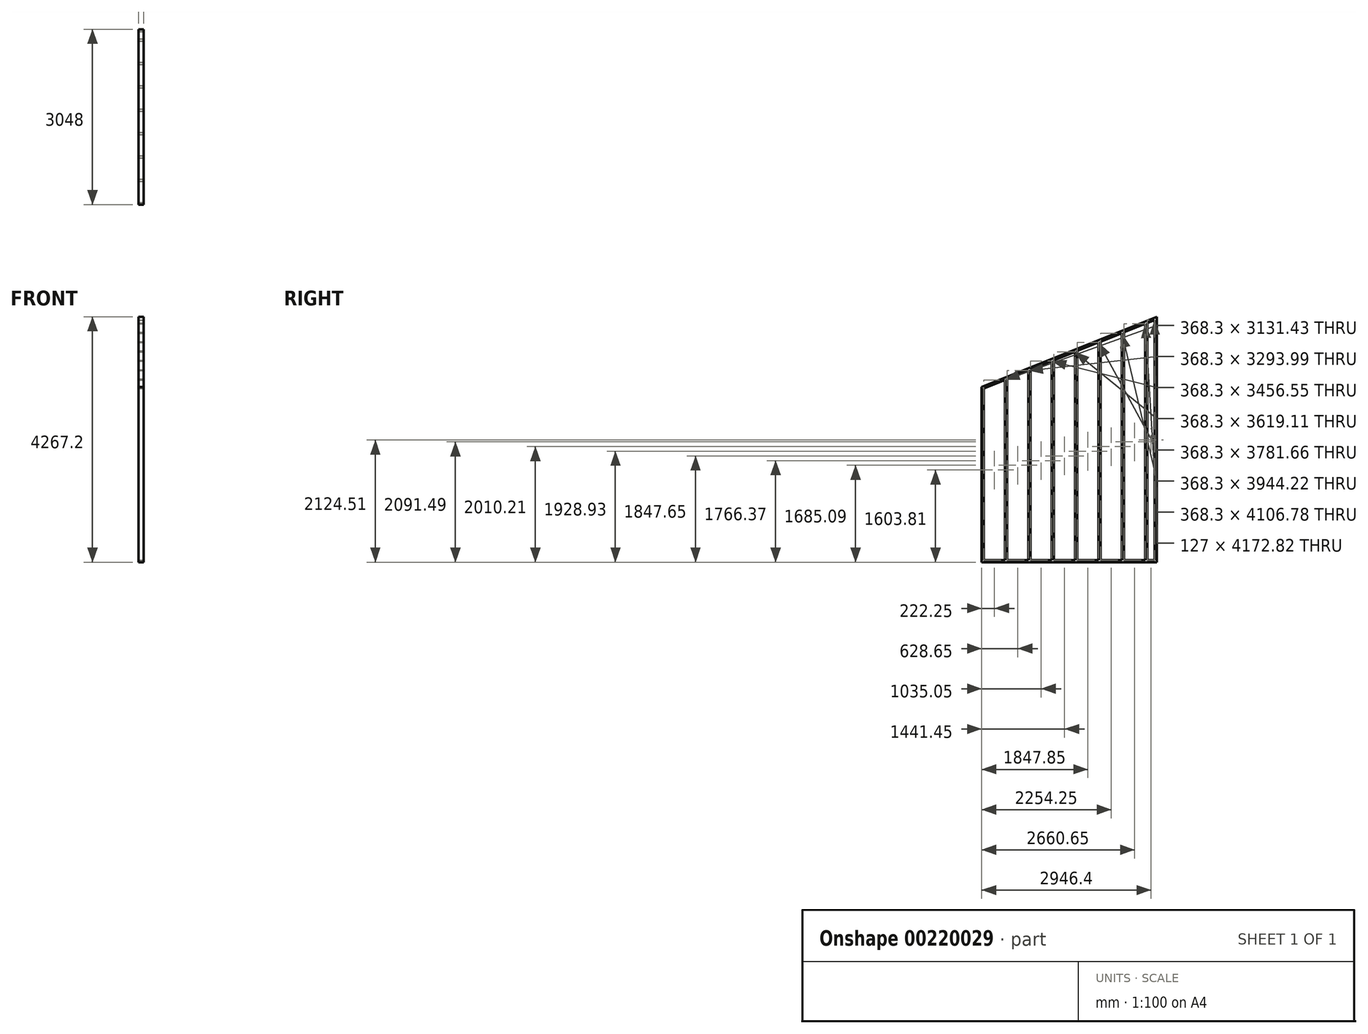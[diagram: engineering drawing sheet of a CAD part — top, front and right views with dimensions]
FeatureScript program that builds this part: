
annotation { "Feature Type Name" : "Feature", "Feature Type Description" : "" }
export const myFeature = defineFeature(function(context is Context, id is Id, definition is map)
    precondition{}
    {
        {
            var Q0;
            Q0=qCreatedBy(makeId("Right.planeOp"),FACE);
            var sketch = newSketch(context, id + "F0", { "sketchPlane" : qUnion([Q0])});
            skLineSegment(sketch, "E0", {"start": v(0, 0) * mm, "end": v(3048, 0) * mm});
            skLineSegment(sketch, "E1", {"start": v(3048, 0) * mm, "end": v(3048, 4267.2) * mm});
            skLineSegment(sketch, "E2", {"start": v(3048, 4267.2) * mm, "end": v(0, 3048) * mm});
            skLineSegment(sketch, "E3", {"start": v(0, 3048) * mm, "end": v(0, 0) * mm});
            skSolve(sketch);
        }
        {
            var Q0;
            Q0=makeQuery(id+"F0.imprint","IMPRINT",FACE,{"disambiguationData":[TD([[makeQuery(id+"F0.imprint","IMPRINT",EDGE,{"derivedFrom":sQuery(id+"F0.wireOp",EDGE,"E0")}),1.0]])]});
            extrude(context, id + "F1", {"entities" : qUnion([Q0]), "depth" : 88.9 * mm});
        }
        {
            var Q0;
            Q0=makeQuery(id+"F1.opExtrude","CAP_FACE",FACE,{"disambiguationData":[OSD([sQuery(id+"F0.wireOp",EDGE,"E0"),sQuery(id+"F0.wireOp",EDGE,"E1"),sQuery(id+"F0.wireOp",EDGE,"E2"),sQuery(id+"F0.wireOp",EDGE,"E3")])],"isStart":false});
            var sketch = newSketch(context, id + "F2", { "sketchPlane" : qUnion([Q0])});
            skLineSegment(sketch, "E4", {"start": v(38.1, 3022.2) * mm, "end": v(38.1, 38.1) * mm});
            skLineSegment(sketch, "E5", {"start": v(38.1, 38.1) * mm, "end": v(406.4, 38.1) * mm});
            skLineSegment(sketch, "E6", {"start": v(406.4, 38.1) * mm, "end": v(406.4, 3169.53) * mm});
            skLineSegment(sketch, "E7", {"start": v(406.4, 3169.53) * mm, "end": v(38.1, 3022.2) * mm});
            skLineSegment(sketch, "E8", {"start": v(444.5, 3184.77) * mm, "end": v(444.5, 38.1) * mm});
            skLineSegment(sketch, "E9", {"start": v(444.5, 38.1) * mm, "end": v(812.8, 38.1) * mm});
            skLineSegment(sketch, "E10", {"start": v(812.8, 38.1) * mm, "end": v(812.8, 3332.09) * mm});
            skLineSegment(sketch, "E11", {"start": v(812.8, 3332.09) * mm, "end": v(444.5, 3184.77) * mm});
            skLineSegment(sketch, "E12", {"start": v(850.9, 3347.33) * mm, "end": v(850.9, 38.1) * mm});
            skLineSegment(sketch, "E13", {"start": v(850.9, 38.1) * mm, "end": v(1219.2, 38.1) * mm});
            skLineSegment(sketch, "E14", {"start": v(1219.2, 38.1) * mm, "end": v(1219.2, 3494.65) * mm});
            skLineSegment(sketch, "E15", {"start": v(1219.2, 3494.65) * mm, "end": v(850.9, 3347.33) * mm});
            skLineSegment(sketch, "E16", {"start": v(1257.3, 3509.89) * mm, "end": v(1257.3, 38.1) * mm});
            skLineSegment(sketch, "E17", {"start": v(1257.3, 38.1) * mm, "end": v(1625.6, 38.1) * mm});
            skLineSegment(sketch, "E18", {"start": v(1625.6, 38.1) * mm, "end": v(1625.6, 3657.2) * mm});
            skLineSegment(sketch, "E19", {"start": v(1625.6, 3657.2) * mm, "end": v(1257.3, 3509.89) * mm});
            skLineSegment(sketch, "E20", {"start": v(1663.7, 3672.45) * mm, "end": v(1663.7, 38.1) * mm});
            skLineSegment(sketch, "E21", {"start": v(1663.7, 38.1) * mm, "end": v(2032, 38.1) * mm});
            skLineSegment(sketch, "E22", {"start": v(2032, 38.1) * mm, "end": v(2032, 3819.77) * mm});
            skLineSegment(sketch, "E23", {"start": v(2032, 3819.77) * mm, "end": v(1663.7, 3672.45) * mm});
            skLineSegment(sketch, "E24", {"start": v(2070.1, 3835) * mm, "end": v(2070.1, 38.1) * mm});
            skLineSegment(sketch, "E25", {"start": v(2070.1, 38.1) * mm, "end": v(2438.4, 38.1) * mm});
            skLineSegment(sketch, "E26", {"start": v(2438.4, 38.1) * mm, "end": v(2438.4, 3982.33) * mm});
            skLineSegment(sketch, "E27", {"start": v(2438.4, 3982.33) * mm, "end": v(2070.1, 3835) * mm});
            skLineSegment(sketch, "E28", {"start": v(2476.5, 3997.57) * mm, "end": v(2476.5, 38.1) * mm});
            skLineSegment(sketch, "E29", {"start": v(2476.5, 38.1) * mm, "end": v(2844.8, 38.1) * mm});
            skLineSegment(sketch, "E30", {"start": v(2844.8, 38.1) * mm, "end": v(2844.8, 4144.89) * mm});
            skLineSegment(sketch, "E31", {"start": v(2844.8, 4144.89) * mm, "end": v(2476.5, 3997.57) * mm});
            skLineSegment(sketch, "E32", {"start": v(2882.9, 4160.13) * mm, "end": v(2882.9, 38.1) * mm});
            skLineSegment(sketch, "E33", {"start": v(2882.9, 38.1) * mm, "end": v(3009.9, 38.1) * mm});
            skLineSegment(sketch, "E34", {"start": v(3009.9, 38.1) * mm, "end": v(3009.9, 4210.93) * mm});
            skLineSegment(sketch, "E35", {"start": v(3009.9, 4210.93) * mm, "end": v(2882.9, 4160.13) * mm});
            skSolve(sketch);
        }
        {
            var Q0;
            Q0=makeQuery(id+"F2.imprint","IMPRINT",FACE,{"disambiguationData":[TD([[makeQuery(id+"F2.imprint","IMPRINT",EDGE,{"derivedFrom":sQuery(id+"F2.wireOp",EDGE,"E4")}),1.0]])]});
            var Q1;
            Q1=makeQuery(id+"F2.imprint","IMPRINT",FACE,{"disambiguationData":[TD([[makeQuery(id+"F2.imprint","IMPRINT",EDGE,{"derivedFrom":sQuery(id+"F2.wireOp",EDGE,"E8")}),1.0]])]});
            var Q2;
            Q2=makeQuery(id+"F2.imprint","IMPRINT",FACE,{"disambiguationData":[TD([[makeQuery(id+"F2.imprint","IMPRINT",EDGE,{"derivedFrom":sQuery(id+"F2.wireOp",EDGE,"E12")}),1.0]])]});
            var Q3;
            Q3=makeQuery(id+"F2.imprint","IMPRINT",FACE,{"disambiguationData":[TD([[makeQuery(id+"F2.imprint","IMPRINT",EDGE,{"derivedFrom":sQuery(id+"F2.wireOp",EDGE,"E16")}),1.0]])]});
            var Q4;
            Q4=makeQuery(id+"F2.imprint","IMPRINT",FACE,{"disambiguationData":[TD([[makeQuery(id+"F2.imprint","IMPRINT",EDGE,{"derivedFrom":sQuery(id+"F2.wireOp",EDGE,"E20")}),1.0]])]});
            var Q5;
            Q5=makeQuery(id+"F2.imprint","IMPRINT",FACE,{"disambiguationData":[TD([[makeQuery(id+"F2.imprint","IMPRINT",EDGE,{"derivedFrom":sQuery(id+"F2.wireOp",EDGE,"E24")}),1.0]])]});
            var Q6;
            Q6=makeQuery(id+"F2.imprint","IMPRINT",FACE,{"disambiguationData":[TD([[makeQuery(id+"F2.imprint","IMPRINT",EDGE,{"derivedFrom":sQuery(id+"F2.wireOp",EDGE,"E28")}),1.0]])]});
            var Q7;
            Q7=makeQuery(id+"F2.imprint","IMPRINT",FACE,{"disambiguationData":[TD([[makeQuery(id+"F2.imprint","IMPRINT",EDGE,{"derivedFrom":sQuery(id+"F2.wireOp",EDGE,"E32")}),1.0]])]});
            extrude(context, id + "F3", {"entities" : qUnion([Q0, Q1, Q2, Q3, Q4, Q5, Q6, Q7]), "operationType" : NewBodyOperationType.REMOVE, "endBound" : BoundingType.THROUGH_ALL, "oppositeDirection" : true, "depth" : 25.4 * mm});
        }
    });
